FCSTD DOCUMENT  (FreeCAD 0.16R)
Label: 4mmfan
License: All rights reserved
LicenseURL: http://en.wikipedia.org/wiki/All_rights_reserved
objects: Sketcher::SketchObject×1
note: 1 computed .brp shape members not serialized (recipe doc carries the construction recipe); baked Part::Feature solids carry a one-line shape summary decoded from their .brp

FEATURE [Sketcher::SketchObject] Sketch
  sketch-geometry (9):
    g0: Circle [constr] CenterX=0 CenterY=0 CenterZ=0 NormalX=0 NormalY=0 NormalZ=1 Radius=18
    g1: Circle [constr] CenterX=-16 CenterY=16 CenterZ=0 NormalX=0 NormalY=0 NormalZ=1 Radius=1.7
    g2: Circle [constr] CenterX=16 CenterY=16 CenterZ=0 NormalX=0 NormalY=0 NormalZ=1 Radius=1.7
    g3: Circle [constr] CenterX=-16 CenterY=-16 CenterZ=0 NormalX=0 NormalY=0 NormalZ=1 Radius=1.7
    g4: Circle [constr] CenterX=16 CenterY=-16 CenterZ=0 NormalX=0 NormalY=0 NormalZ=1 Radius=1.7
    g5: LineSegment [constr] StartX=-20 StartY=20 StartZ=0 EndX=20 EndY=20 EndZ=0
    g6: LineSegment [constr] StartX=20 StartY=20 StartZ=0 EndX=20 EndY=-20 EndZ=0
    g7: LineSegment [constr] StartX=20 StartY=-20 StartZ=0 EndX=-20 EndY=-20 EndZ=0
    g8: LineSegment [constr] StartX=-20 StartY=-20 StartZ=0 EndX=-20 EndY=20 EndZ=0
  constraints (24):
    c: Coincident(g0,g-1)
    c: Radius(g0) = 18
    c: Symmetric(g1,g2,g-2)
    c: Equal(g1,g2)
    c: Equal(g2,g3)
    c: Equal(g3,g4)
    c: Symmetric(g1,g3,g-1)
    c: Symmetric(g3,g4,g-2)
    c: Radius(g1) = 1.7
    c: DistanceX(g1,g2) = 32
    c: DistanceY(g3,g1) = 32
    c: Coincident(g5,g6)
    c: Coincident(g6,g7)
    c: Coincident(g7,g8)
    c: Coincident(g8,g5)
    c: Horizontal(g5)
    c: Horizontal(g7)
    c: Vertical(g6)
    c: Vertical(g8)
    c: Equal(g5,g8)
    c: Equal(g8,g6)
    c: Equal(g6,g7)
    c: Symmetric(g5,g6,g-1)
    c: DistanceX(g7,g7) = 40
